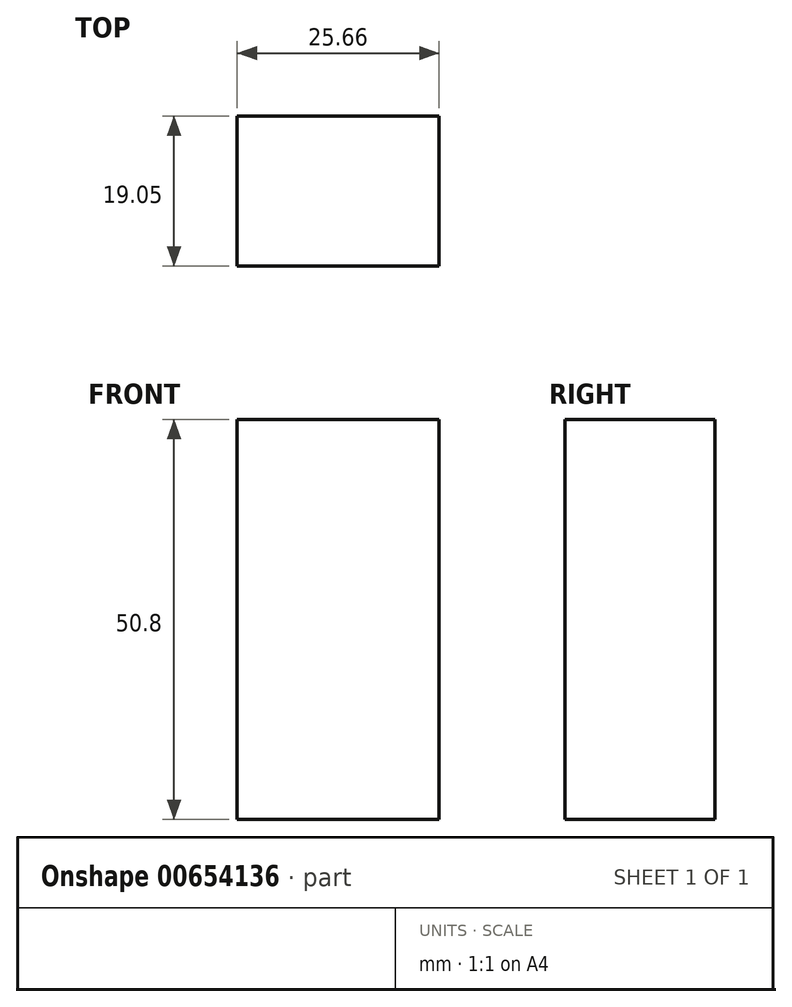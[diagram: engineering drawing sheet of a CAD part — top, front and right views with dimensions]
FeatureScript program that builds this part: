
annotation { "Feature Type Name" : "Feature", "Feature Type Description" : "" }
export const myFeature = defineFeature(function(context is Context, id is Id, definition is map)
    precondition{}
    {
        {
            var Q0;
            Q0=qCreatedBy(makeId("Front.planeOp"),FACE);
            var sketch = newSketch(context, id + "F0", { "sketchPlane" : qUnion([Q0])});
            skLineSegment(sketch, "E0.bottom", {"start": v(-12.83, 25.4) * mm, "end": v(12.83, 25.4) * mm});
            skLineSegment(sketch, "E0.top", {"start": v(-12.83, -25.4) * mm, "end": v(12.83, -25.4) * mm});
            skLineSegment(sketch, "E0.left", {"start": v(-12.83, 25.4) * mm, "end": v(-12.83, -25.4) * mm});
            skLineSegment(sketch, "E0.right", {"start": v(12.83, 25.4) * mm, "end": v(12.83, -25.4) * mm});
            skPoint(sketch, "E0.middle", {"position": v(0, 0) * mm});
            skSolve(sketch);
        }
        {
            var Q0;
            Q0=qSketchRegion(id+"F0",true);
            extrude(context, id + "F1", {"entities" : qUnion([Q0]), "depth" : 19.05 * mm, "offsetDistance" : 25.4 * mm});
        }
    });
